# Revit family: P1I_2903-2943-2606_OS275
name_source: partatom
category: Porte
units: mm (PartAtom-declared; Revit-internal decimal feet)

## family parameters
Condiviso = No
Host = Muro
Numero OmniClass = 23.30.10.00
Punto di calcolo locali = Sì
Sempre verticale = Sì
Taglio con vuoti quando caricato = No
Titolo OmniClass = Doors

## types (4) — shared parameters
Chiusura muro = Per host
Costruzione analitica = <Nessuno>
Descrizione = Porta ad un'anta, apertura interna
Funzione = Interno
H_Max = 2900 mm  [stored 9.51444 ft]
H_Min = 1600 mm
H_maniglia = 1000 mm  [stored 3.28084 ft]
L_Max = 1000 mm  [stored 3.28084 ft]
L_Min = 400 mm  [stored 1.31234 ft]
Larghezza telaio = 75 mm
Modello = OS2 75
Produttore = Secco Sistemi Spa
Proiezione telaio est. = 25 mm  [stored 0.082021 ft]
Proiezione telaio int. = 25 mm  [stored 0.082021 ft]
URL = https://www.seccosistemi.com
WARNING = No
n2_cerniere = 2
n3_cerniere = 3
n4_cerniere = 4
numero_cerniere = 3

## per-type parameters (varying)
| type | Altezza | H | H1 | H_vetro | L | L1 | L_vetro | Larghezza | MATERIALE |
| Acciaio Zincato | 2000 mm  [stored 6.56168 ft] | 2000 mm  [stored 6.56168 ft] | 2000 mm  [stored 6.56168 ft] | 1924 mm | 900 mm  [stored 2.95276 ft] | 900 mm  [stored 2.95276 ft] | 824 mm  [stored 2.70341 ft] | 900 mm  [stored 2.95276 ft] | Acciaio |
| Acciaio Inox | 2000 mm  [stored 6.56168 ft] | 2000 mm  [stored 6.56168 ft] | 2000 mm  [stored 6.56168 ft] | 1924 mm | 900 mm  [stored 2.95276 ft] | 900 mm  [stored 2.95276 ft] | 824 mm  [stored 2.70341 ft] | 900 mm  [stored 2.95276 ft] | Acciaio inox, spazzolato |
| Acciaio Corten | 2900 mm  [stored 9.51444 ft] | 2900 mm  [stored 9.51444 ft] | 2900 mm  [stored 9.51444 ft] | 2824 mm | 1000 mm  [stored 3.28084 ft] | 1000 mm  [stored 3.28084 ft] | 924 mm | 1000 mm  [stored 3.28084 ft] | Acciaio corten |
| Ottone | 2000 mm  [stored 6.56168 ft] | 2000 mm  [stored 6.56168 ft] | 2000 mm  [stored 6.56168 ft] | 1924 mm | 900 mm  [stored 2.95276 ft] | 900 mm  [stored 2.95276 ft] | 824 mm  [stored 2.70341 ft] | 900 mm  [stored 2.95276 ft] | Ottone |

note: [stored X ft] marks values corroborated as IEEE doubles in the binary element streams (Revit-internal decimal feet)
